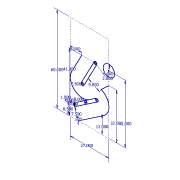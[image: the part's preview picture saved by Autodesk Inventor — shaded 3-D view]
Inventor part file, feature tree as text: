
AUTODESK INVENTOR PART (.ipt)
format: ipt  version: 2012 (Build 160160000, 160)  size: 81,920 bytes
history: native  units: in
note: dims shown in document units (in); Inventor stores cm internally (conversion verified against a paired STEP export)
features: sketch x1
ambient origin geometry x8: Origin, YZ Plane, XZ Plane, XY Plane, X Axis, Y Axis, Z Axis, Center Point
feature tree (1):
  sketch  "Sketch1"  dims[d0=27.0in d1=60.0in d2=2.0in d3=7.5in d4=1.0in d5=1.0in d6=8.5in d7=0.375in d8=2.0in d9=8.0in d10=41.0in d11=32.0in d12=12.0in d13=9.0in d14=7.5in d15=41.0in d16=2.0in d17=8.0in]
